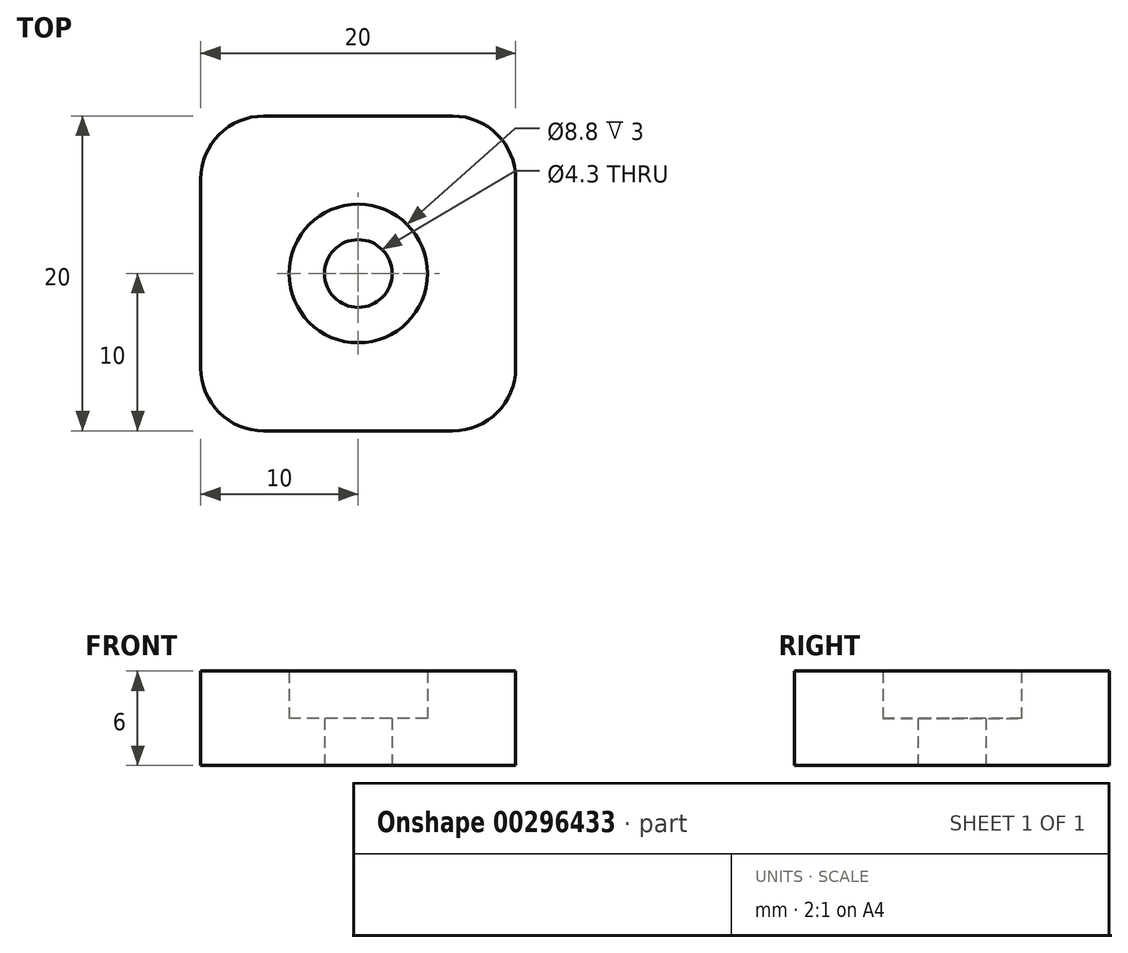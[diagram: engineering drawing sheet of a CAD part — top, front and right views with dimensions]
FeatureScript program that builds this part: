
annotation { "Feature Type Name" : "Feature", "Feature Type Description" : "" }
export const myFeature = defineFeature(function(context is Context, id is Id, definition is map)
    precondition{}
    {
        {
            var Q0;
            Q0=qCreatedBy(makeId("Top.planeOp"),FACE);
            var sketch = newSketch(context, id + "F0", { "sketchPlane" : qUnion([Q0])});
            skLineSegment(sketch, "E0.bottom", {"start": v(10, -10) * mm, "end": v(-10, -10) * mm});
            skLineSegment(sketch, "E0.top", {"start": v(10, 10) * mm, "end": v(-10, 10) * mm});
            skLineSegment(sketch, "E0.left", {"start": v(10, -10) * mm, "end": v(10, 10) * mm});
            skLineSegment(sketch, "E0.right", {"start": v(-10, -10) * mm, "end": v(-10, 10) * mm});
            skPoint(sketch, "E0.middle", {"position": v(0, 0) * mm});
            skCircle(sketch, "E1", {"center": v(0, 0) * mm, "radius": 2.15 * mm});
            skCircle(sketch, "E2", {"center": v(0, 0) * mm, "radius": 4.4 * mm});
            skSolve(sketch);
        }
        {
            var Q0;
            Q0=makeQuery(id+"F0.imprint","IMPRINT",FACE,{"disambiguationData":[TD([[makeQuery(id+"F0.imprint","IMPRINT",EDGE,{"derivedFrom":sQuery(id+"F0.wireOp",EDGE,"E0.bottom")}),-1.0]])]});
            extrude(context, id + "F1", {"entities" : qUnion([Q0]), "depth" : 6 * mm});
        }
        {
            var Q0;
            Q0=makeQuery(id+"F0.imprint","IMPRINT",FACE,{"disambiguationData":[TD([[makeQuery(id+"F0.imprint","IMPRINT",EDGE,{"derivedFrom":sQuery(id+"F0.wireOp",EDGE,"E1")}),-1.0]])]});
            extrude(context, id + "F2", {"entities" : qUnion([Q0]), "operationType" : NewBodyOperationType.ADD, "depth" : 3 * mm});
        }
        {
            var Q0;
            Q0=makeQuery(id+"F1.opExtrude","SWEPT_EDGE",EDGE,{"disambiguationData":[OSD([sQuery(id+"F0.wireOp",EDGE,"E0.bottom"),sQuery(id+"F0.wireOp",EDGE,"E0.left")])]});
            var Q1;
            Q1=makeQuery(id+"F1.opExtrude","SWEPT_EDGE",EDGE,{"disambiguationData":[OSD([sQuery(id+"F0.wireOp",EDGE,"E0.top"),sQuery(id+"F0.wireOp",EDGE,"E0.left")])]});
            var Q2;
            Q2=makeQuery(id+"F1.opExtrude","SWEPT_EDGE",EDGE,{"disambiguationData":[OSD([sQuery(id+"F0.wireOp",EDGE,"E0.top"),sQuery(id+"F0.wireOp",EDGE,"E0.right")])]});
            var Q3;
            Q3=makeQuery(id+"F1.opExtrude","SWEPT_EDGE",EDGE,{"disambiguationData":[OSD([sQuery(id+"F0.wireOp",EDGE,"E0.bottom"),sQuery(id+"F0.wireOp",EDGE,"E0.right")])]});
            fillet(context, id + "F3", {"entities" : qUnion([Q0, Q1, Q2, Q3]), "radius" : 4 * mm, "tangentPropagation" : true, "allowEdgeOverflow" : false});
        }
    });
